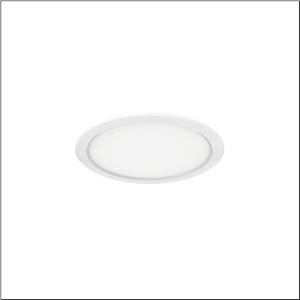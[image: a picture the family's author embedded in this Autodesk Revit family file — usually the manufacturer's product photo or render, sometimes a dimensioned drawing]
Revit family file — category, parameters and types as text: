
# Revit family: lunis_41_eco_51ds107f44a
name_source: partatom
category: Lighting Fixtures
units: mm (PartAtom-declared; Revit-internal decimal feet)

## family parameters
Cut with Voids When Loaded = No
Host = Face
Light Source = No
Part Type = Normal
Room Calculation Point = No
Round Connector Dimension = Use Diameter
Shared = No

## types (1)
- Lunis 41 ECO (1 x LED, 2300 lm, 22 W, 4000K)
    Apparent Load = 22 VA
    CIE Flux Codes = 47 80 97 100 100
    Color Rendering = 80
    Color Temperature = 4000K
    Default Elevation = 1800 mm
    Description = Lunis 41,  ECO, downlight, light emission: direct distribution, LED rated luminous flux: 2.300lm, light colour: 840, control gear: ECG, mains connection: 230V, AC, 50/60Hz, housing, round, of aluminium, coated, traffic white (RAL 9016), diameter: 216mm, recess depth: 58mm, protection rating (complete): IP20, protection rating (on room side): IP40, insulation class (complete): insulation class II (safety insulation), certification: CE, permissible ambient temperature for indoor applications: -20..+40°C, packaging unit: 1 piece
    Height = 0 mm  [stored 0 ft]
    Lamp = 1 x LED
    Lamp Light Flux = 2300 lm
    Lamp Power = 22 W
    Lamp count = 1
    Length = 216 mm
    Luminous efficacy = 105 lm/W
    Manufacturer = Siteco
    ModVariant = No
    Model = 51DS107F44A
    Mounting Place = Ceiling
    Mounting Type = Recessed
    Number of Poles = 1
    OnlyDefault = Yes
    Power Factor = 1
    Product Name = Lunis 41 ECO
    Product group = downlight
    ProductGroupID = 400
    Protection Class = Protection class II
    Protection Degree = IP 20
    RLX_Detail_Level = 1
    RLX_Emergency_Light_Flux = 0 lm
    RLX_Emergency_Type = 0
    RLX_Emergency_Type_DB = No
    RlxData = <blob elided: 22789 chars, md5=736e51a3>
    Socket = socket
    Standby Power = 0 W
    System Light Flux = 2300 lm
    System Power = 22 W
    Type Comments = Product without accessories
    Type Image = l_1007043.jpg
    URL = http://relux.com
    VarID = ---
    Voltage = 0 V
    Weight = 0.00 kg
    Width = 0 mm  [stored 0 ft]

note: [stored X ft] marks values corroborated as IEEE doubles in the binary element streams (Revit-internal decimal feet)

## geometry (parser evidence)
native form markers: Blend x4, Sweep x10
no freeform markers — native parametric forms only
